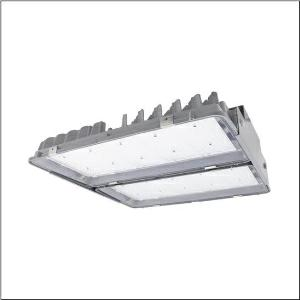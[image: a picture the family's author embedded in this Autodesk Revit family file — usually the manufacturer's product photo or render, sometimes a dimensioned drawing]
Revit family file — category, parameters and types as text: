
# Revit family: highbay_11xtreme_51hf62db4qma
name_source: partatom
category: Lighting Fixtures
units: mm (PartAtom-declared; Revit-internal decimal feet)

## family parameters
Cut with Voids When Loaded = No
Host = Face
Light Source = No
Part Type = Normal
Room Calculation Point = No
Round Connector Dimension = Use Diameter
Shared = No

## types (1)
- --- (1 x LED, 36800 lm, 193.7 W, 4000K)
    Apparent Load = 194 VA
    CIE Flux Codes = 84 96 100 100 100
    Color Rendering = 80
    Color Temperature = 4000K
    Default Elevation = 1800 mm
    Description = Highbay 11Xtreme, LED high bay luminaire, primary light control with lens, of PMMA, primary optical cover: cover, of toughened safety glass, light emission: direct distribution, primary light characteristic: symmetric, installation type: suspended mounting, surface-mounted, 2x LED module,for 1x 2x LED, rated luminous flux: 36.000lm, luminous efficacy: 178lm/W, light colour: 840, colour temperature: 4000K, with cable H07RN-F 5x 1.5mm², mains connection: 220..240V, AC, 50/60Hz, cable length: 1,5m, rated input power: 202W, luminaire housing, of diecast aluminium, coated, silver, length: 595mm, width: 560mm, height: 195mm, protection rating (complete): IP66, insulation class (complete): insulation class I (protective earthing), certification: CE, ENEC, UKCA, protection symbol: D, ball protection: ball impact resistant according to DIN VDE 0710 part 13 (with chain suspension), impact resistance: IK08, permissible operating ambient temperature: -25..+70°C, reducing of maximum allowable ambient temperature of 5°C with ceiling mounting, packaging unit: 1 piece
    Height = 157 mm
    Lamp = 1 x LED
    Lamp Light Flux = 36800 lm
    Lamp Power = 193.7 W
    Lamp count = 1
    Length = 593 mm
    Luminous efficacy = 190 lm/W
    Manufacturer = Siteco
    ModVariant = No
    Model = 51HF62DB4QMA
    Mounting Place = Ceiling
    Mounting Type = Pendant
    Number of Poles = 1
    OnlyDefault = Yes
    Power Factor = 1
    Product Name = Highbay 11Xtreme
    Product group = LED high bay luminaire
    ProductGroupID = 903
    Protection Class = Protection class I
    Protection Degree = IP 66
    RLX_Detail_Level = 1
    RLX_Emergency_Light_Flux = 0 lm
    RLX_Emergency_Type = 0
    RLX_Emergency_Type_DB = No
    RlxData = <blob elided: 34309 chars, md5=3d97c3ff>
    Socket = socket
    Standby Power = 0 W
    System Light Flux = 36799 lm
    System Power = 194 W
    Type Comments = factory setting: luminous flux: 100 % | dim-lin: 254 | 648 mA
    Type Image = l_1258340.jpg
    URL = http://relux.com
    VarID = @adj_035671
    Voltage = 0 V
    Weight = 0.00 kg
    Width = 568 mm

## geometry (parser evidence)
native form markers: Blend x4, Sweep x10
no freeform markers — native parametric forms only
